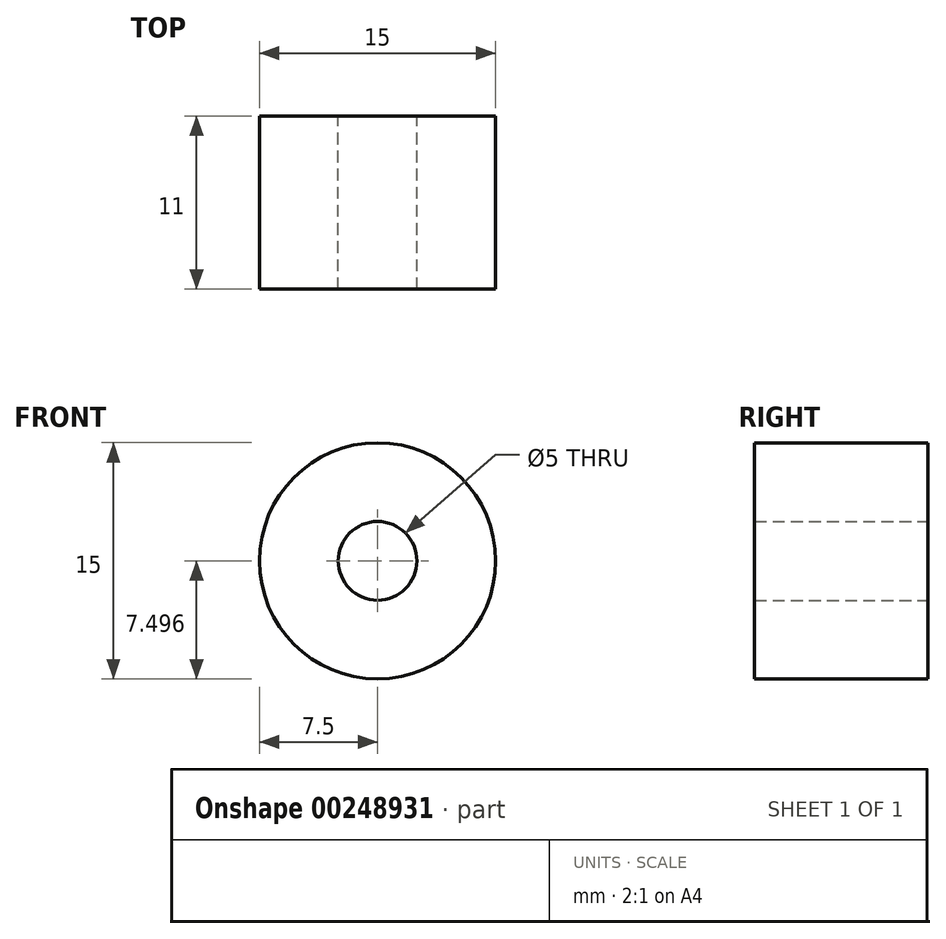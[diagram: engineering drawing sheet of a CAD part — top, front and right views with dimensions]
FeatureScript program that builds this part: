
annotation { "Feature Type Name" : "Feature", "Feature Type Description" : "" }
export const myFeature = defineFeature(function(context is Context, id is Id, definition is map)
    precondition{}
    {
        {
            var Q0;
            Q0=qCreatedBy(makeId("Front.planeOp"),FACE);
            var sketch = newSketch(context, id + "F0", { "sketchPlane" : qUnion([Q0])});
            skArc(sketch, "E0", {"start": v(-41.17, 47.16) * mm, "mid": v(-30.07, -22.2) * mm, "end": v(-18.97, 47.16) * mm});
            skCircle(sketch, "E1", {"center": v(-30.07, 52.72) * mm, "radius": 2 * mm});
            skArc(sketch, "E2", {"start": v(-41.17, 47.16) * mm, "mid": v(-30.07, 46.37) * mm, "end": v(-18.97, 47.16) * mm});
            skCircle(sketch, "E3", {"center": v(-30.07, 13.37) * mm, "radius": 1.5 * mm});
            skLineSegment(sketch, "E4", {"start": v(-30.07, 13.37) * mm, "end": v(-30.07, 60.7) * mm});
            skArc(sketch, "E5", {"start": v(-30.07, 56.28) * mm, "mid": v(-36.97, 53.36) * mm, "end": v(-41.17, 47.16) * mm});
            skPoint(sketch, "E5.startSnap0", {"position": v(-29.45, 56.36) * mm});
            skArc(sketch, "E6.MirrorCS", {"start": v(-30.07, 56.28) * mm, "mid": v(-23.17, 53.36) * mm, "end": v(-18.97, 47.16) * mm});
            skPoint(sketch, "E7.orphan", {"position": v(-31.45, 56.36) * mm});
            skPoint(sketch, "E8.orphan", {"position": v(-28.69, 56.36) * mm});
            skCircle(sketch, "E9", {"center": v(-30.07, 13.37) * mm, "radius": 7.5 * mm});
            skCircle(sketch, "E10", {"center": v(-30.07, 13.37) * mm, "radius": 2.5 * mm});
            skSolve(sketch);
        }
        {
            var Q0;
            {var subQ0=sQuery(id+"F0.wireOp",EDGE,"E0");Q0=makeQuery(id+"F0.imprint","IMPRINT",FACE,{"disambiguationData":[TD([[makeQuery(id+"F0.imprint","IMPRINT",EDGE,{"derivedFrom":subQ0}),1.0]])]});}
            extrude(context, id + "F1", {"entities" : qUnion([Q0]), "depth" : 8 * mm});
        }
        {
            var Q0;
            {var subQ0=sQuery(id+"F0.wireOp",EDGE,"E5");Q0=makeQuery(id+"F0.imprint","IMPRINT",FACE,{"disambiguationData":[TD([[makeQuery(id+"F0.imprint","IMPRINT",EDGE,{"derivedFrom":subQ0}),1.0]])]});}
            var Q1;
            {var subQ0=sQuery(id+"F0.wireOp",EDGE,"E6.MirrorCS");Q1=makeQuery(id+"F0.imprint","IMPRINT",FACE,{"disambiguationData":[TD([[makeQuery(id+"F0.imprint","IMPRINT",EDGE,{"derivedFrom":subQ0}),-1.0]])]});}
            extrude(context, id + "F2", {"entities" : qUnion([Q0, Q1]), "operationType" : NewBodyOperationType.ADD, "depth" : 3 * mm});
        }
        {
            var Q0;
            Q0=makeQuery(id+"F1.opExtrude","SWEPT_BODY",BODY,{"disambiguationData":[OSD([sQuery(id+"F0.wireOp",EDGE,"E0"),sQuery(id+"F0.wireOp",EDGE,"E2"),sQuery(id+"F0.wireOp",EDGE,"E9")])]});
            deleteBodies(context, id + "F3", {"entities" : qUnion([Q0])});
        }
        {
            var Q0;
            Q0=makeQuery(id+"F0.imprint","IMPRINT",FACE,{"disambiguationData":[TD([[makeQuery(id+"F0.imprint","IMPRINT",EDGE,{"derivedFrom":sQuery(id+"F0.wireOp",EDGE,"E9")}),1.0]])]});
            extrude(context, id + "F4", {"entities" : qUnion([Q0]), "depth" : 11 * mm});
        }
    });
